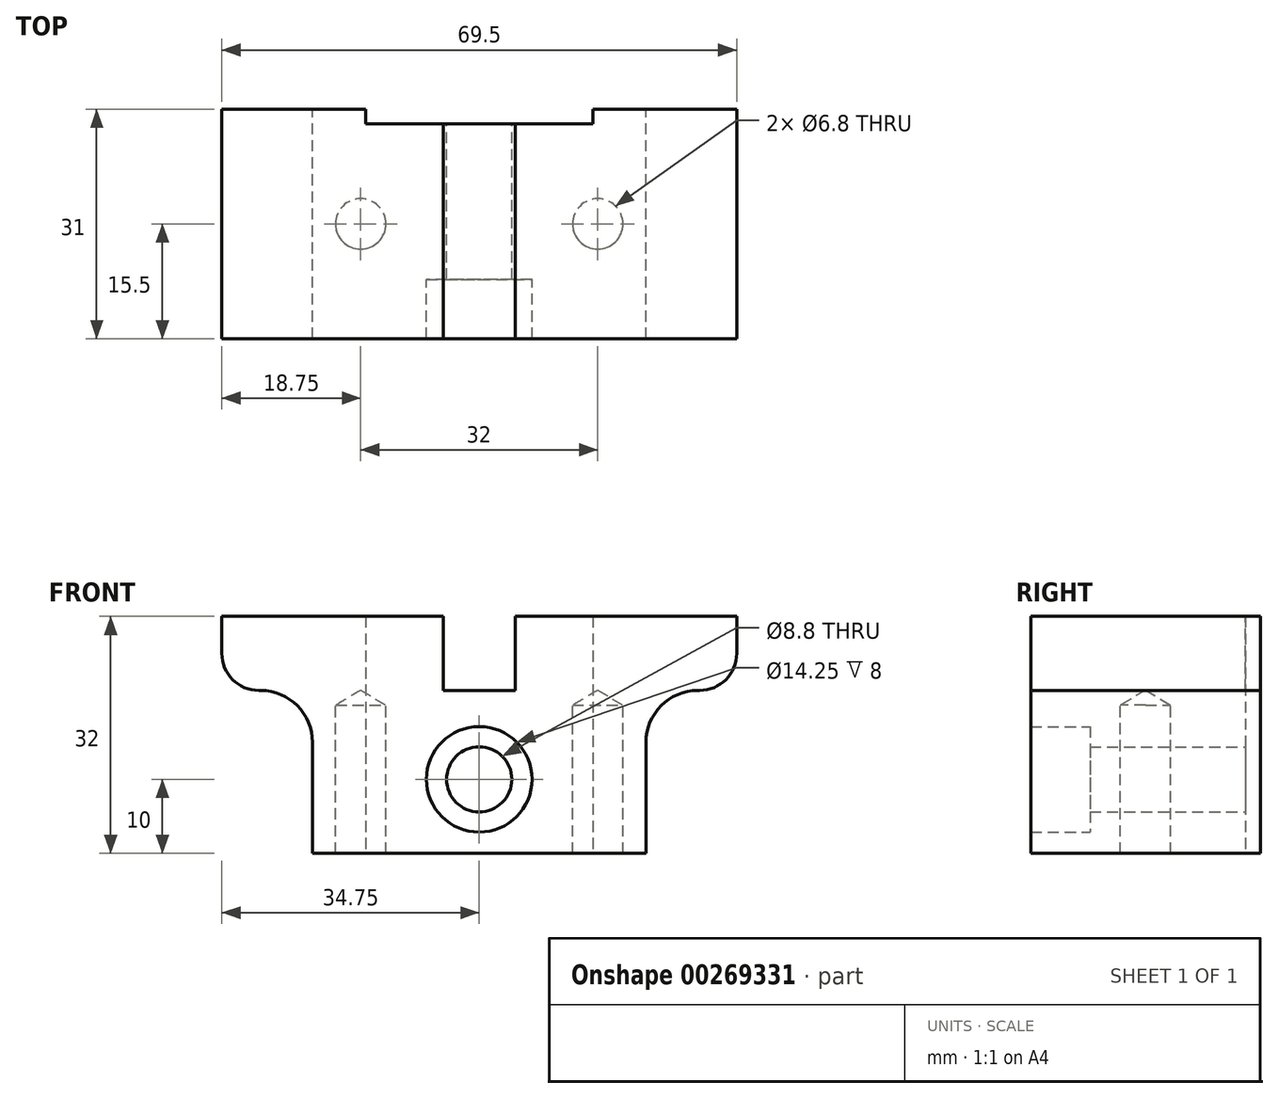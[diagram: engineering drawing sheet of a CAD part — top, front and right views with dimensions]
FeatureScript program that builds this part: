
annotation { "Feature Type Name" : "Feature", "Feature Type Description" : "" }
export const myFeature = defineFeature(function(context is Context, id is Id, definition is map)
    precondition{}
    {
        {
            var Q0;
            Q0=qCreatedBy(makeId("Front.planeOp"),FACE);
            var sketch = newSketch(context, id + "F0", { "sketchPlane" : qUnion([Q0])});
            skLineSegment(sketch, "E0", {"start": v(-34.75, 32) * mm, "end": v(-4.88, 32) * mm});
            skLineSegment(sketch, "E1", {"start": v(34.75, 32) * mm, "end": v(34.75, 27) * mm});
            skLineSegment(sketch, "E2", {"start": v(22.5, 15) * mm, "end": v(22.5, 0) * mm});
            skLineSegment(sketch, "E3", {"start": v(22.5, 0) * mm, "end": v(-22.5, 0) * mm});
            skLineSegment(sketch, "E4", {"start": v(-22.5, 0) * mm, "end": v(-22.5, 15) * mm});
            skLineSegment(sketch, "E5", {"start": v(-34.75, 27) * mm, "end": v(-34.75, 32) * mm});
            skLineSegment(sketch, "E6", {"start": v(0, 32) * mm, "end": v(0, 0) * mm, "construction": true});
            skLineSegment(sketch, "E7", {"start": v(29.75, 22) * mm, "end": v(29.5, 22) * mm});
            skLineSegment(sketch, "E8", {"start": v(-29.75, 22) * mm, "end": v(-29.5, 22) * mm});
            skPoint(sketch, "E9.visualSharp", {"position": v(34.75, 22) * mm});
            skArc(sketch, "E9.filletArc", {"start": v(29.75, 22) * mm, "mid": v(33.29, 23.46) * mm, "end": v(34.75, 27) * mm});
            skPoint(sketch, "E10.visualSharp", {"position": v(-34.75, 22) * mm});
            skArc(sketch, "E10.filletArc", {"start": v(-34.75, 27) * mm, "mid": v(-33.29, 23.46) * mm, "end": v(-29.75, 22) * mm});
            skPoint(sketch, "E11.visualSharp", {"position": v(-22.5, 22) * mm});
            skArc(sketch, "E11.filletArc", {"start": v(-22.5, 15) * mm, "mid": v(-24.55, 19.95) * mm, "end": v(-29.5, 22) * mm});
            skPoint(sketch, "E12.visualSharp", {"position": v(22.5, 22) * mm});
            skArc(sketch, "E12.filletArc", {"start": v(29.5, 22) * mm, "mid": v(24.55, 19.95) * mm, "end": v(22.5, 15) * mm});
            skLineSegment(sketch, "E13", {"start": v(-4.88, 32) * mm, "end": v(-4.88, 22) * mm});
            skLineSegment(sketch, "E14", {"start": v(-4.88, 22) * mm, "end": v(4.88, 22) * mm});
            skLineSegment(sketch, "E15", {"start": v(4.87, 22) * mm, "end": v(4.87, 32) * mm});
            skLineSegment(sketch, "E16.trimOffspring", {"start": v(4.88, 32) * mm, "end": v(34.75, 32) * mm});
            skSolve(sketch);
        }
        {
            var Q0;
            Q0=makeQuery(id+"F0.imprint","IMPRINT",FACE,{"disambiguationData":[TD([[makeQuery(id+"F0.imprint","IMPRINT",EDGE,{"derivedFrom":sQuery(id+"F0.wireOp",EDGE,"E0")}),-1.0]])]});
            extrude(context, id + "F1", {"entities" : qUnion([Q0]), "depth" : 31 * mm});
        }
        {
            var Q0;
            Q0=makeQuery(id+"F1.opExtrude","CAP_FACE",FACE,{"disambiguationData":[OSD([sQuery(id+"F0.wireOp",EDGE,"E0"),sQuery(id+"F0.wireOp",EDGE,"E1"),sQuery(id+"F0.wireOp",EDGE,"E2"),sQuery(id+"F0.wireOp",EDGE,"E3"),sQuery(id+"F0.wireOp",EDGE,"E4"),sQuery(id+"F0.wireOp",EDGE,"E5"),sQuery(id+"F0.wireOp",EDGE,"E7"),sQuery(id+"F0.wireOp",EDGE,"E8"),sQuery(id+"F0.wireOp",EDGE,"E9.filletArc"),sQuery(id+"F0.wireOp",EDGE,"E10.filletArc"),sQuery(id+"F0.wireOp",EDGE,"E11.filletArc"),sQuery(id+"F0.wireOp",EDGE,"E12.filletArc"),sQuery(id+"F0.wireOp",EDGE,"E13"),sQuery(id+"F0.wireOp",EDGE,"E14"),sQuery(id+"F0.wireOp",EDGE,"E15"),sQuery(id+"F0.wireOp",EDGE,"E16.trimOffspring")])],"isStart":true});
            var sketch = newSketch(context, id + "F2", { "sketchPlane" : qUnion([Q0])});
            skLineSegment(sketch, "E17.bottom", {"start": v(15.32, 32) * mm, "end": v(-15.33, 32) * mm});
            skLineSegment(sketch, "E17.top", {"start": v(15.33, 0) * mm, "end": v(-15.32, 0) * mm});
            skLineSegment(sketch, "E17.left", {"start": v(15.32, 32) * mm, "end": v(15.33, 0) * mm});
            skLineSegment(sketch, "E17.right", {"start": v(-15.33, 32) * mm, "end": v(-15.32, 0) * mm});
            skPoint(sketch, "E17.middle", {"position": v(0, 16) * mm});
            skSolve(sketch);
        }
        {
            var Q0;
            Q0=makeQuery(id+"F2.imprint","IMPRINT",FACE,{"disambiguationData":[TD([[makeQuery(id+"F2.imprint","IMPRINT",EDGE,{"derivedFrom":sQuery(id+"F2.wireOp",EDGE,"E17.top")}),1.0]])]});
            extrude(context, id + "F3", {"entities" : qUnion([Q0]), "operationType" : NewBodyOperationType.REMOVE, "oppositeDirection" : true, "depth" : 2 * mm});
        }
        {
            var Q0;
            Q0=makeQuery(id+"F1.opExtrude","SWEPT_FACE",FACE,{"disambiguationData":[OSD([sQuery(id+"F0.wireOp",EDGE,"E3")])]});
            var sketch = newSketch(context, id + "F4", { "sketchPlane" : qUnion([Q0])});
            skLineSegment(sketch, "E18", {"start": v(-22.5, 15.5) * mm, "end": v(22.5, 15.5) * mm, "construction": true});
            skPoint(sketch, "E19", {"position": v(-16, 15.5) * mm});
            skPoint(sketch, "E20", {"position": v(16, 15.5) * mm});
            skLineSegment(sketch, "E21", {"start": v(0, 31) * mm, "end": v(0, 0) * mm, "construction": true});
            skSolve(sketch);
        }
        {
            var Q0;
            Q0=sQuery(id+"F4.wireOp",VERTEX,"E19");
            var Q1;
            Q1=sQuery(id+"F4.wireOp",VERTEX,"E20");
            var Q2;
            Q2=makeQuery(id+"F1.opExtrude","SWEPT_BODY",BODY,{"disambiguationData":[OSD([sQuery(id+"F0.wireOp",EDGE,"E0"),sQuery(id+"F0.wireOp",EDGE,"E1"),sQuery(id+"F0.wireOp",EDGE,"E2"),sQuery(id+"F0.wireOp",EDGE,"E3"),sQuery(id+"F0.wireOp",EDGE,"E4"),sQuery(id+"F0.wireOp",EDGE,"E5"),sQuery(id+"F0.wireOp",EDGE,"E7"),sQuery(id+"F0.wireOp",EDGE,"E8"),sQuery(id+"F0.wireOp",EDGE,"E9.filletArc"),sQuery(id+"F0.wireOp",EDGE,"E10.filletArc"),sQuery(id+"F0.wireOp",EDGE,"E11.filletArc"),sQuery(id+"F0.wireOp",EDGE,"E12.filletArc"),sQuery(id+"F0.wireOp",EDGE,"E13"),sQuery(id+"F0.wireOp",EDGE,"E14"),sQuery(id+"F0.wireOp",EDGE,"E15"),sQuery(id+"F0.wireOp",EDGE,"E16.trimOffspring")])]});
            hole(context, id + "F5", {"style" : HoleStyle.SIMPLE, "endStyle" : HoleEndStyle.BLIND, "standardTappedOrClearance" : lookupTablePath({ "standard" : "ISO", "engagement" : "75%", "pitch" : "1.25 mm", "size" : "M8", "type" : "Tapped" }), "standardBlindInLast" : lookupTablePath({ "standard" : "ISO", "engagement" : "75%", "pitch" : "1.25 mm", "size" : "M8", "type" : "Tapped" }), "holeDiameter" : 6.8 * mm, "holeDepth" : 20 * mm, "locations" : qUnion([Q0, Q1]), "scope" : qUnion([Q2]), "majorDiameter" : 8 * mm});
        }
        {
            var Q0;
            Q0=makeQuery(id+"F1.opExtrude","CAP_FACE",FACE,{"disambiguationData":[OSD([sQuery(id+"F0.wireOp",EDGE,"E0"),sQuery(id+"F0.wireOp",EDGE,"E1"),sQuery(id+"F0.wireOp",EDGE,"E2"),sQuery(id+"F0.wireOp",EDGE,"E3"),sQuery(id+"F0.wireOp",EDGE,"E4"),sQuery(id+"F0.wireOp",EDGE,"E5"),sQuery(id+"F0.wireOp",EDGE,"E7"),sQuery(id+"F0.wireOp",EDGE,"E8"),sQuery(id+"F0.wireOp",EDGE,"E9.filletArc"),sQuery(id+"F0.wireOp",EDGE,"E10.filletArc"),sQuery(id+"F0.wireOp",EDGE,"E11.filletArc"),sQuery(id+"F0.wireOp",EDGE,"E12.filletArc"),sQuery(id+"F0.wireOp",EDGE,"E13"),sQuery(id+"F0.wireOp",EDGE,"E14"),sQuery(id+"F0.wireOp",EDGE,"E15"),sQuery(id+"F0.wireOp",EDGE,"E16.trimOffspring")])],"isStart":false});
            var sketch = newSketch(context, id + "F6", { "sketchPlane" : qUnion([Q0])});
            skLineSegment(sketch, "E22", {"start": v(-22.5, 10) * mm, "end": v(22.5, 10) * mm, "construction": true});
            skPoint(sketch, "E23", {"position": v(0, 10) * mm});
            skSolve(sketch);
        }
        {
            var Q0;
            Q0=sQuery(id+"F6.wireOp",VERTEX,"E23");
            var Q1;
            Q1=makeQuery(id+"F1.opExtrude","SWEPT_BODY",BODY,{"disambiguationData":[OSD([sQuery(id+"F0.wireOp",EDGE,"E0"),sQuery(id+"F0.wireOp",EDGE,"E1"),sQuery(id+"F0.wireOp",EDGE,"E2"),sQuery(id+"F0.wireOp",EDGE,"E3"),sQuery(id+"F0.wireOp",EDGE,"E4"),sQuery(id+"F0.wireOp",EDGE,"E5"),sQuery(id+"F0.wireOp",EDGE,"E7"),sQuery(id+"F0.wireOp",EDGE,"E8"),sQuery(id+"F0.wireOp",EDGE,"E9.filletArc"),sQuery(id+"F0.wireOp",EDGE,"E10.filletArc"),sQuery(id+"F0.wireOp",EDGE,"E11.filletArc"),sQuery(id+"F0.wireOp",EDGE,"E12.filletArc"),sQuery(id+"F0.wireOp",EDGE,"E13"),sQuery(id+"F0.wireOp",EDGE,"E14"),sQuery(id+"F0.wireOp",EDGE,"E15"),sQuery(id+"F0.wireOp",EDGE,"E16.trimOffspring")])]});
            hole(context, id + "F7", {"style" : HoleStyle.C_BORE, "endStyle" : HoleEndStyle.THROUGH, "standardTappedOrClearance" : lookupTablePath({ "standard" : "ISO", "fit" : "Normal", "size" : "M8", "type" : "Clearance" }), "standardBlindInLast" : lookupTablePath({ "fit" : "Standard", "standard" : "ISO", "size" : "M8", "type" : "Clearance" }), "holeDiameter" : 8.8 * mm, "cBoreDiameter" : 14.25 * mm, "cBoreDepth" : 8 * mm, "locations" : qUnion([Q0]), "scope" : qUnion([Q1]), "isTappedThrough" : true});
        }
    });
